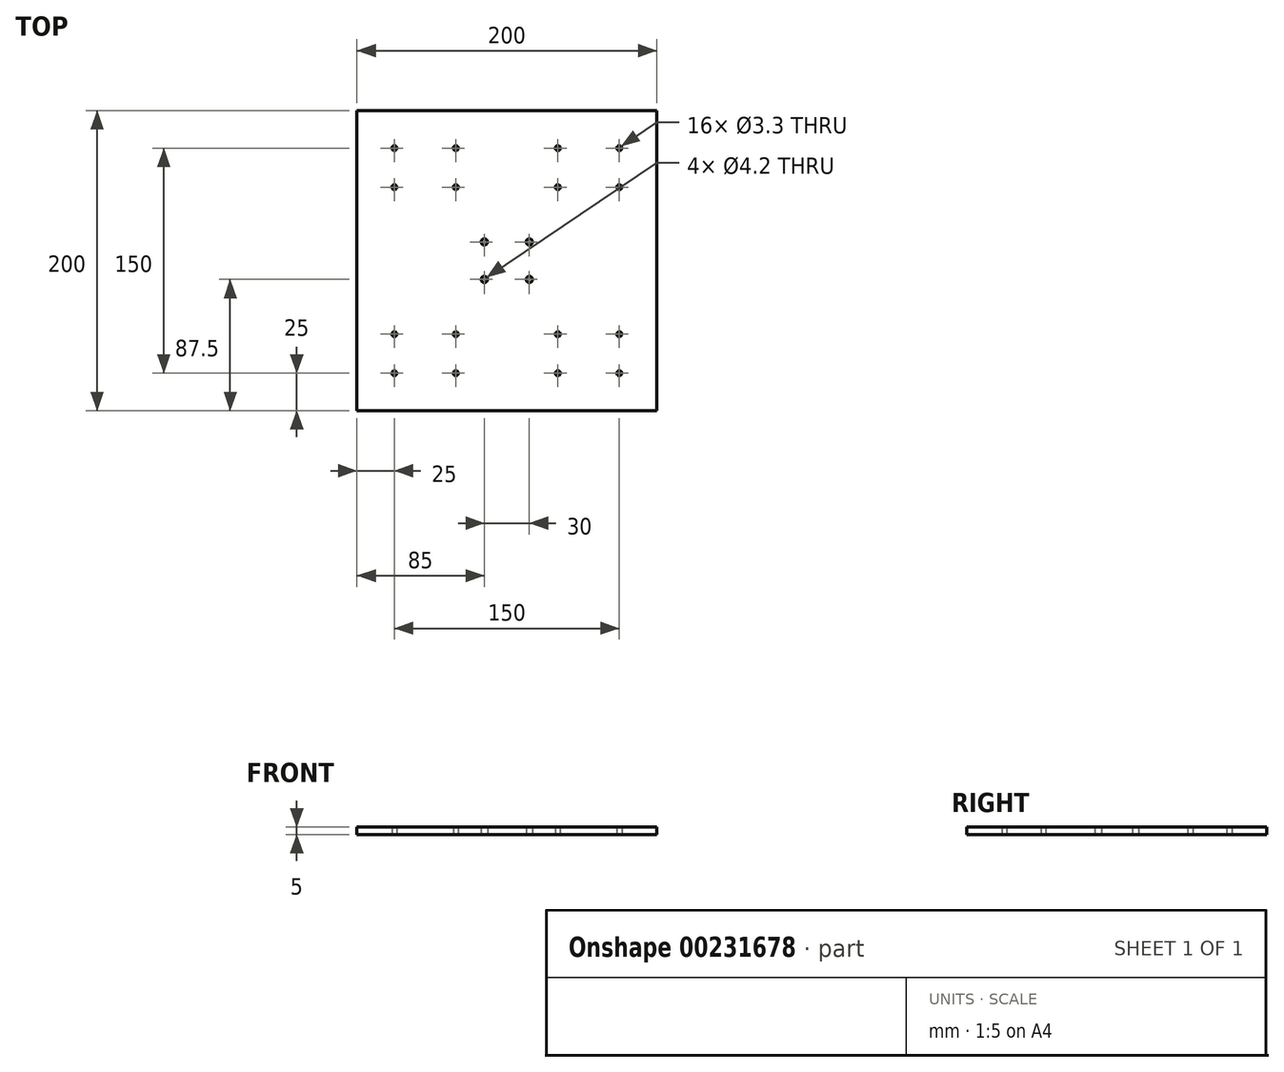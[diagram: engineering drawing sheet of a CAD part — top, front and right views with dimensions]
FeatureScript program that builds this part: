
annotation { "Feature Type Name" : "Feature", "Feature Type Description" : "" }
export const myFeature = defineFeature(function(context is Context, id is Id, definition is map)
    precondition{}
    {
        {
            var Q0;
            Q0=qCreatedBy(makeId("Top.planeOp"),FACE);
            var sketch = newSketch(context, id + "F0", { "sketchPlane" : qUnion([Q0])});
            skLineSegment(sketch, "E0.bottom", {"start": v(100, 100) * mm, "end": v(-100, 100) * mm});
            skLineSegment(sketch, "E0.top", {"start": v(100, -100) * mm, "end": v(-100, -100) * mm});
            skLineSegment(sketch, "E0.left", {"start": v(100, 100) * mm, "end": v(100, -100) * mm});
            skLineSegment(sketch, "E0.right", {"start": v(-100, 100) * mm, "end": v(-100, -100) * mm});
            skPoint(sketch, "E0.middle", {"position": v(0, 0) * mm});
            skCircle(sketch, "E1", {"center": v(-15, 12.5) * mm, "radius": 2.1 * mm});
            skCircle(sketch, "E2", {"center": v(-75, 75) * mm, "radius": 1.65 * mm});
            skCircle(sketch, "E3", {"center": v(-34, 75) * mm, "radius": 1.65 * mm});
            skCircle(sketch, "E4", {"center": v(-75, 49) * mm, "radius": 1.65 * mm});
            skCircle(sketch, "E5", {"center": v(-34, 49) * mm, "radius": 1.65 * mm});
            skCircle(sketch, "E6.MirrorC", {"center": v(34, 49) * mm, "radius": 1.65 * mm});
            skCircle(sketch, "E7.MirrorC", {"center": v(15, 12.5) * mm, "radius": 2.1 * mm});
            skCircle(sketch, "E8.MirrorC", {"center": v(75, 75) * mm, "radius": 1.65 * mm});
            skCircle(sketch, "E9.MirrorC", {"center": v(34, 75) * mm, "radius": 1.65 * mm});
            skCircle(sketch, "E10.MirrorC", {"center": v(75, 49) * mm, "radius": 1.65 * mm});
            skCircle(sketch, "E11.MirrorC", {"center": v(75, -49) * mm, "radius": 1.65 * mm});
            skCircle(sketch, "E12.MirrorC", {"center": v(34, -75) * mm, "radius": 1.65 * mm});
            skCircle(sketch, "E13.MirrorC", {"center": v(75, -75) * mm, "radius": 1.65 * mm});
            skCircle(sketch, "E14.MirrorC", {"center": v(15, -12.5) * mm, "radius": 2.1 * mm});
            skCircle(sketch, "E15.MirrorC", {"center": v(34, -49) * mm, "radius": 1.65 * mm});
            skCircle(sketch, "E16.MirrorC", {"center": v(-15, -12.5) * mm, "radius": 2.1 * mm});
            skCircle(sketch, "E17.MirrorC", {"center": v(-34, -49) * mm, "radius": 1.65 * mm});
            skCircle(sketch, "E18.MirrorC", {"center": v(-75, -49) * mm, "radius": 1.65 * mm});
            skCircle(sketch, "E19.MirrorC", {"center": v(-34, -75) * mm, "radius": 1.65 * mm});
            skCircle(sketch, "E20.MirrorC", {"center": v(-75, -75) * mm, "radius": 1.65 * mm});
            skSolve(sketch);
        }
        {
            var Q0;
            Q0 = qSketchRegion(id + "F0", true);
            extrude(context, id + "F1", {"entities" : qUnion([Q0]), "depth" : 5 * mm});
        }
    });
